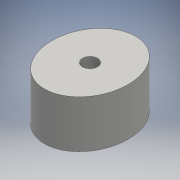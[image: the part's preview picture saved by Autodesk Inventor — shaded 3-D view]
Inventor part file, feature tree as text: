
AUTODESK INVENTOR PART (.ipt)
format: ipt  version: 2016 (Build 200138000, 138)  size: 176,128 bytes
history: native  units: mm
features: extrude x1, sketch x1
ambient origin geometry x8: Origin, YZ Plane, XZ Plane, XY Plane, X Axis, Y Axis, Z Axis, Center Point
bodies: Solid1 (feature_tree)
feature tree (2):
  extrude  "Extrusion1"  Depth=5.0mm
  sketch  "Sketch1"  dims[d0=4.8mm d1=4.0mm d2=1.5875mm d3=5.0mm d4=0.0mm]
